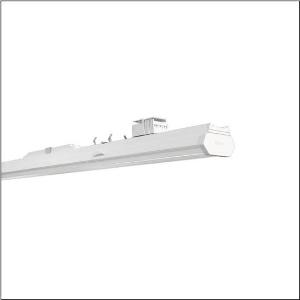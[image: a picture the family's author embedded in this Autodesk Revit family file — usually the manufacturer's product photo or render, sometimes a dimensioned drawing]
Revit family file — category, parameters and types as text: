
# Revit family: licross_r__21_protected_ho_52td11dn4e5s_21e0
name_source: partatom
category: Lighting Fixtures
units: mm (PartAtom-declared; Revit-internal decimal feet)

## family parameters
Cut with Voids When Loaded = No
Host = Face
Light Source = No
Part Type = Normal
Room Calculation Point = No
Round Connector Dimension = Use Diameter
Shared = No

## types (1)
- --- (1 x LED, 14920 lm, 84.9 W, 4000K)
    Apparent Load = 85 VA
    CIE Flux Codes = 84 94 98 99 100
    Color Rendering = 80
    Color Temperature = 4000K
    Default Elevation = 1800 mm
    Description = Licross® 21 Protected HO, luminaire insert, of sheet steel, galvanised, coil coated, white, length: 1.500mm, width: 90mm, height: 103mm, LED rated luminous flux: 14.920lm, light colour: 840, control gear: DALI 2, with plug, 5-pole, with phase selection, mains connection: 220..240V, AC, 50/60Hz, rated input power: 85W, halogen-free wiring, primary light control with lens, of plastic, primary optical cover: cover, of PMMA, light emission: direct distribution, primary light characteristic: symmetric, protection rating (complete): IP54, insulation class (complete): insulation class I (protective earthing), certification: CE, ENEC, VDE, UKCA, protection symbol: D if used in an environment with non-conductive dust loads with corresponding accessories, impact resistance: IK06, permissible ambient temperature for indoor applications: -25..+35°C, corresponds to IFS (International Featured Standards) requirements for safety and quality in the food industry, reducing of maximum allowable ambient temperature of 5°C with ceiling mounting, LABS conformity tested according to VDMA 24364:2018-05, packaging unit: 1 piece
    Height = 92 mm
    Lamp = 1 x LED
    Lamp Light Flux = 14920 lm
    Lamp Power = 84.9 W
    Lamp count = 1
    Length = 1500 mm
    Luminous efficacy = 176 lm/W
    Manufacturer = Siteco
    ModVariant = No
    Model = 52TD11DN4E5S
    Mounting Place = Ceiling
    Mounting Type = Pendant
    Number of Poles = 1
    OnlyDefault = Yes
    Power Factor = 1
    Product Name = Licross® 21 Protected HO
    Product group = luminaire insert
    ProductGroupID = 901
    Protection Class = Protection class I
    Protection Degree = IP 54
    RLX_Detail_Level = 1
    RLX_Emergency_Light_Flux = 0 lm
    RLX_Emergency_Type = 0
    RLX_Emergency_Type_DB = No
    RlxData = <blob elided: 24409 chars, md5=24c0a9ae>
    Socket = socket
    Standby Power = 0 W
    System Light Flux = 14920 lm
    System Power = 85 W
    Type Comments = factory setting: luminous flux: 100 % | dim-lin: 254 | 484 mA
    Type Image = l_1256148.jpg
    URL = http://relux.com
    VarID = @adj_060159
    Voltage = 0 V
    Weight = 0.00 kg
    Width = 88 mm

## geometry (parser evidence)
native form markers: Blend x4, Sweep x12
no freeform markers — native parametric forms only
